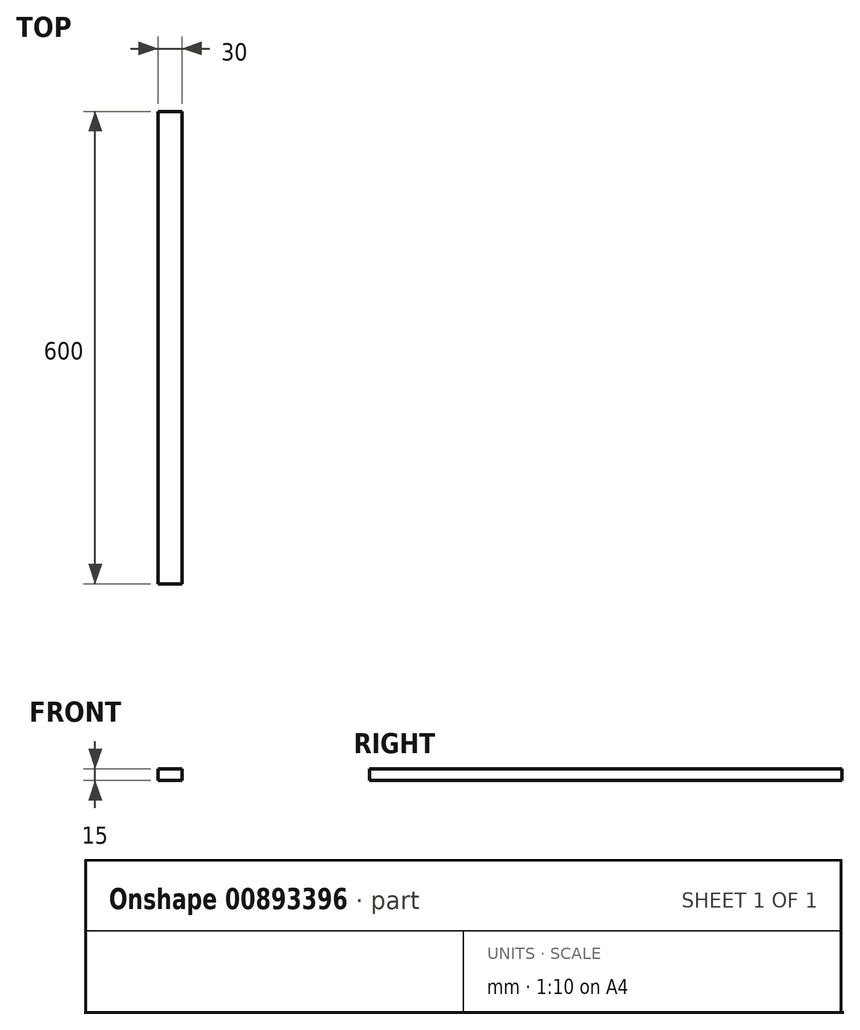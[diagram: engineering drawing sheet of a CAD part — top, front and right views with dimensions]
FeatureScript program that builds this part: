
annotation { "Feature Type Name" : "Feature", "Feature Type Description" : "" }
export const myFeature = defineFeature(function(context is Context, id is Id, definition is map)
    precondition{}
    {
        {
            var Q0;
            Q0=qCreatedBy(makeId("Front.planeOp"),FACE);
            var sketch = newSketch(context, id + "F0", { "sketchPlane" : qUnion([Q0])});
            skLineSegment(sketch, "E0.bottom", {"start": v(0, 0) * mm, "end": v(30, 0) * mm});
            skLineSegment(sketch, "E0.top", {"start": v(0, 15) * mm, "end": v(30, 15) * mm});
            skLineSegment(sketch, "E0.left", {"start": v(0, 0) * mm, "end": v(0, 15) * mm});
            skLineSegment(sketch, "E0.right", {"start": v(30, 0) * mm, "end": v(30, 15) * mm});
            skSolve(sketch);
        }
        {
            var Q0;
            Q0=makeQuery(id+"F0.imprint","IMPRINT",FACE,{"disambiguationData":[TD([[makeQuery(id+"F0.imprint","IMPRINT",EDGE,{"derivedFrom":sQuery(id+"F0.wireOp",EDGE,"E0.bottom")}),1.0]])]});
            extrude(context, id + "F1", {"entities" : qUnion([Q0]), "depth" : 600 * mm, "offsetDistance" : 25 * mm});
        }
    });
